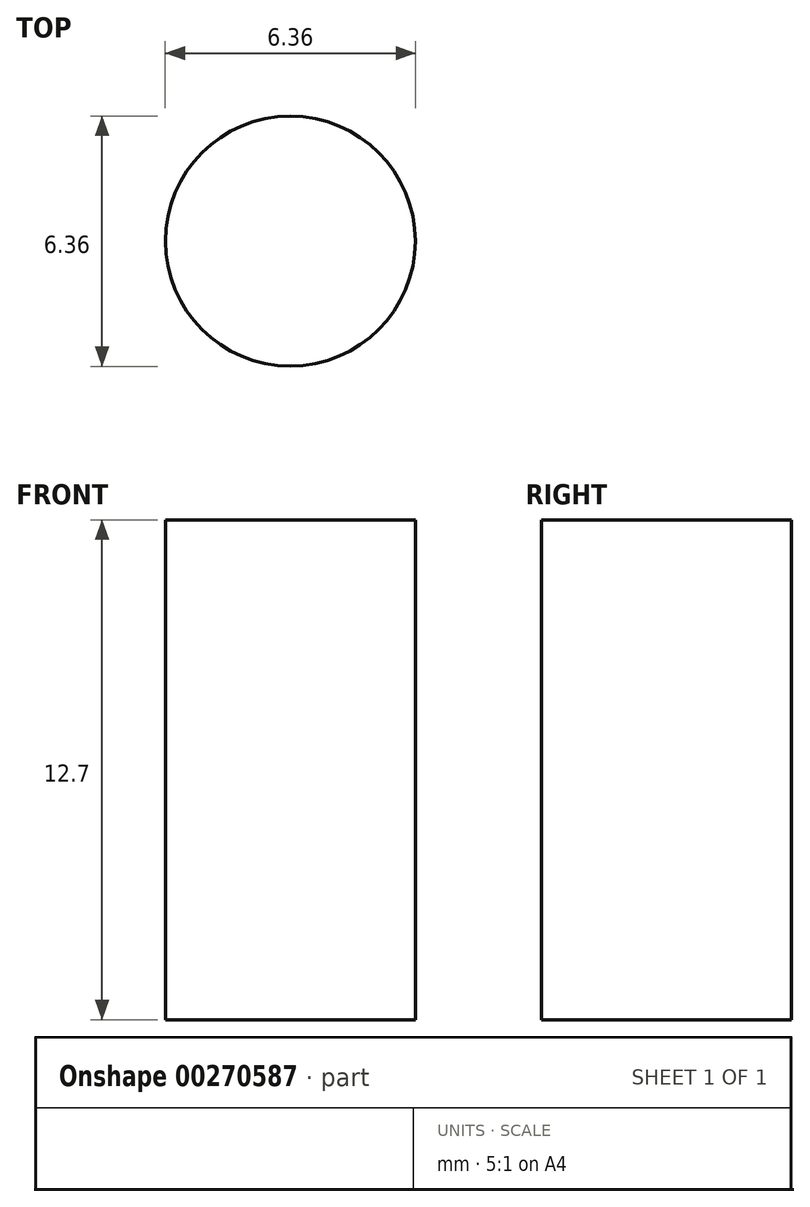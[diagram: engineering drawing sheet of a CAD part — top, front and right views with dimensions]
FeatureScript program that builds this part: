
annotation { "Feature Type Name" : "Feature", "Feature Type Description" : "" }
export const myFeature = defineFeature(function(context is Context, id is Id, definition is map)
    precondition{}
    {
        {
            var Q0;
            Q0=qCreatedBy(makeId("Top.planeOp"),FACE);
            var sketch = newSketch(context, id + "F0", { "sketchPlane" : qUnion([Q0])});
            skCircle(sketch, "E0", {"center": v(0, 0) * mm, "radius": 3.18 * mm});
            skSolve(sketch);
        }
        {
            var Q0;
            Q0=makeQuery(id+"F0.imprint","IMPRINT",FACE,{"disambiguationData":[TD([[makeQuery(id+"F0.imprint","IMPRINT",EDGE,{"derivedFrom":sQuery(id+"F0.wireOp",EDGE,"E0")}),1.0]])]});
            extrude(context, id + "F1", {"entities" : qUnion([Q0]), "depth" : 12.7 * mm});
        }
    });
